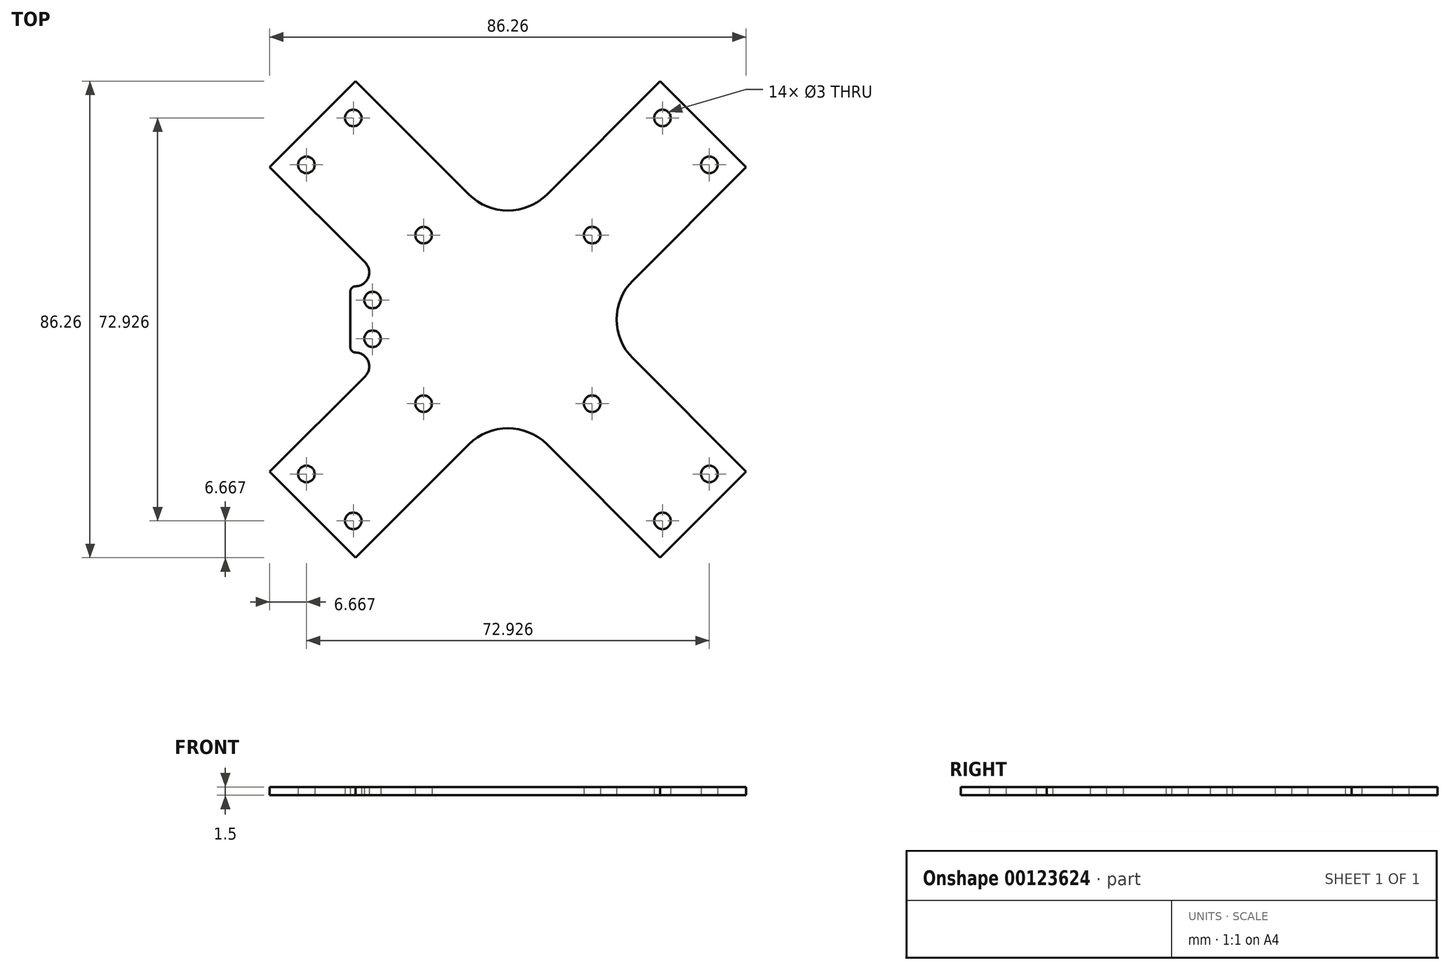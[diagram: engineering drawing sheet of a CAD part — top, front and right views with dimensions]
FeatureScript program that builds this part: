
annotation { "Feature Type Name" : "Feature", "Feature Type Description" : "" }
export const myFeature = defineFeature(function(context is Context, id is Id, definition is map)
    precondition{}
    {
        {
            var Q0;
            Q0=qCreatedBy(makeId("Top.planeOp"),FACE);
            var sketch = newSketch(context, id + "F0", { "sketchPlane" : qUnion([Q0])});
            skCircle(sketch, "E0", {"center": v(-15.25, 15.25) * mm, "radius": 1.5 * mm});
            skCircle(sketch, "E1.0.1.0", {"center": v(-15.25, -15.25) * mm, "radius": 1.5 * mm});
            skCircle(sketch, "E1.1.0.0", {"center": v(15.25, 15.25) * mm, "radius": 1.5 * mm});
            skCircle(sketch, "E1.1.1.0", {"center": v(15.25, -15.25) * mm, "radius": 1.5 * mm});
            skLineSegment(sketch, "E1.direction1", {"start": v(-15.25, 15.25) * mm, "end": v(15.25, 15.25) * mm, "construction": true});
            skLineSegment(sketch, "E1.direction2", {"start": v(-15.25, 15.25) * mm, "end": v(-15.25, -15.25) * mm, "construction": true});
            skLineSegment(sketch, "E2", {"start": v(-42.43, -42.43) * mm, "end": v(42.43, 42.43) * mm, "construction": true});
            skLineSegment(sketch, "E3", {"start": v(-42.43, 42.43) * mm, "end": v(42.43, -42.43) * mm, "construction": true});
            skLineSegment(sketch, "E4", {"start": v(-43.13, 27.58) * mm, "end": v(-27.58, 43.13) * mm});
            skLineSegment(sketch, "E5", {"start": v(-27.58, 43.13) * mm, "end": v(-7.07, 22.63) * mm});
            skPoint(sketch, "E5.endSnap0", {"position": v(0, 15.25) * mm});
            skLineSegment(sketch, "E6", {"start": v(7.07, 22.63) * mm, "end": v(27.58, 43.13) * mm});
            skLineSegment(sketch, "E7", {"start": v(27.58, 43.13) * mm, "end": v(43.13, 27.58) * mm});
            skLineSegment(sketch, "E8", {"start": v(43.13, 27.58) * mm, "end": v(22.63, 7.07) * mm});
            skLineSegment(sketch, "E9", {"start": v(22.63, -7.07) * mm, "end": v(43.13, -27.58) * mm});
            skLineSegment(sketch, "E10", {"start": v(43.13, -27.58) * mm, "end": v(27.58, -43.13) * mm});
            skLineSegment(sketch, "E11", {"start": v(27.58, -43.13) * mm, "end": v(7.07, -22.63) * mm});
            skLineSegment(sketch, "E12", {"start": v(-7.07, -22.63) * mm, "end": v(-27.58, -43.13) * mm});
            skLineSegment(sketch, "E13", {"start": v(-27.58, -43.13) * mm, "end": v(-43.13, -27.58) * mm});
            skLineSegment(sketch, "E14", {"start": v(-43.13, -27.58) * mm, "end": v(-25.82, -10.27) * mm});
            skLineSegment(sketch, "E15", {"start": v(-25.82, 10.27) * mm, "end": v(-43.13, 27.58) * mm});
            skLineSegment(sketch, "E16", {"start": v(-36.46, 27.98) * mm, "end": v(-27.98, 36.46) * mm, "construction": true});
            skLineSegment(sketch, "E17", {"start": v(27.98, 36.46) * mm, "end": v(36.46, 27.98) * mm, "construction": true});
            skLineSegment(sketch, "E18", {"start": v(-36.46, -27.98) * mm, "end": v(-27.98, -36.46) * mm, "construction": true});
            skLineSegment(sketch, "E19", {"start": v(27.98, -36.46) * mm, "end": v(36.46, -27.98) * mm, "construction": true});
            skCircle(sketch, "E20", {"center": v(-36.46, -27.98) * mm, "radius": 1.5 * mm});
            skCircle(sketch, "E21", {"center": v(-27.98, -36.46) * mm, "radius": 1.5 * mm});
            skCircle(sketch, "E22", {"center": v(27.98, -36.46) * mm, "radius": 1.5 * mm});
            skCircle(sketch, "E23", {"center": v(36.46, -27.98) * mm, "radius": 1.5 * mm});
            skCircle(sketch, "E24", {"center": v(36.46, 27.98) * mm, "radius": 1.5 * mm});
            skCircle(sketch, "E25", {"center": v(27.98, 36.46) * mm, "radius": 1.5 * mm});
            skCircle(sketch, "E26", {"center": v(-27.98, 36.46) * mm, "radius": 1.5 * mm});
            skCircle(sketch, "E27", {"center": v(-36.46, 27.98) * mm, "radius": 1.5 * mm});
            skArc(sketch, "E28", {"start": v(-7.07, 22.63) * mm, "mid": v(0, 19.7) * mm, "end": v(7.07, 22.63) * mm});
            skPoint(sketch, "E29.orphan", {"position": v(0, 15.56) * mm});
            skArc(sketch, "E30", {"start": v(7.07, -22.63) * mm, "mid": v(0, -19.7) * mm, "end": v(-7.07, -22.63) * mm});
            skPoint(sketch, "E31.orphan", {"position": v(0, -15.56) * mm});
            skLineSegment(sketch, "E32", {"start": v(-28.5, 5.1) * mm, "end": v(-28.5, -5.1) * mm});
            skPoint(sketch, "E33.orphan", {"position": v(-15.56, 0) * mm});
            skArc(sketch, "E34", {"start": v(-25.82, -10.27) * mm, "mid": v(-25.28, -7.54) * mm, "end": v(-27.6, -6) * mm});
            skArc(sketch, "E35", {"start": v(-27.6, 6) * mm, "mid": v(-25.28, 7.54) * mm, "end": v(-25.82, 10.27) * mm});
            skLineSegment(sketch, "E36", {"start": v(-24.5, 3.5) * mm, "end": v(-24.5, -3.5) * mm, "construction": true});
            skCircle(sketch, "E37", {"center": v(-24.5, 3.5) * mm, "radius": 1.5 * mm});
            skCircle(sketch, "E38", {"center": v(-24.5, -3.5) * mm, "radius": 1.5 * mm});
            skArc(sketch, "E39", {"start": v(-27.6, 6) * mm, "mid": v(-28.23, 5.73) * mm, "end": v(-28.5, 5.1) * mm});
            skArc(sketch, "E40", {"start": v(-28.5, -5.1) * mm, "mid": v(-28.23, -5.73) * mm, "end": v(-27.6, -6) * mm});
            skPoint(sketch, "E41.start.orphan", {"position": v(-28.5, -6) * mm});
            skPoint(sketch, "E42.end.orphan", {"position": v(-28.5, 6) * mm});
            skArc(sketch, "E43", {"start": v(22.63, 7.07) * mm, "mid": v(19.7, 0) * mm, "end": v(22.63, -7.07) * mm});
            skPoint(sketch, "E44.orphan", {"position": v(15.56, 0) * mm});
            skSolve(sketch);
        }
        {
            var Q0;
            Q0 = qSketchRegion(id + "F0", true);
            extrude(context, id + "F1", {"entities" : qUnion([Q0]), "depth" : 1.5 * mm});
        }
    });
